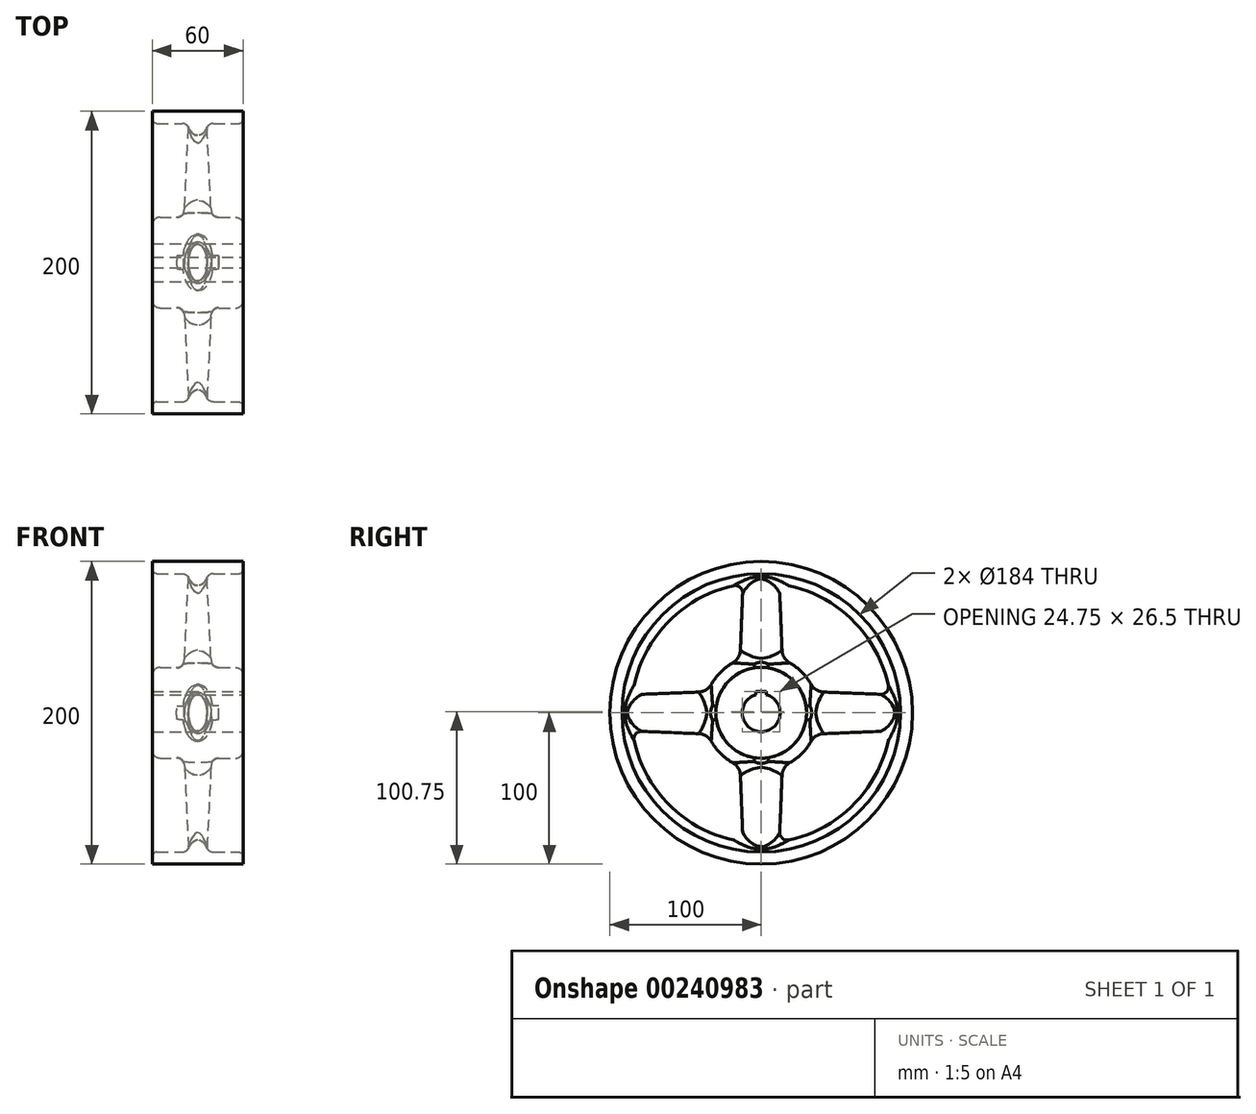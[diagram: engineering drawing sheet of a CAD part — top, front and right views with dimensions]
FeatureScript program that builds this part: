
annotation { "Feature Type Name" : "Feature", "Feature Type Description" : "" }
export const myFeature = defineFeature(function(context is Context, id is Id, definition is map)
    precondition{}
    {
        {
            var Q0;
            Q0=qCreatedBy(makeId("Front.planeOp"),FACE);
            var sketch = newSketch(context, id + "F0", { "sketchPlane" : qUnion([Q0])});
            skLineSegment(sketch, "E0", {"start": v(-30, 12.5) * mm, "end": v(30, 12.5) * mm});
            skLineSegment(sketch, "E1", {"start": v(30, 12.5) * mm, "end": v(30, 30) * mm});
            skLineSegment(sketch, "E2", {"start": v(30, 30) * mm, "end": v(10.58, 30) * mm});
            skLineSegment(sketch, "E3", {"start": v(-30, 30) * mm, "end": v(-30, 12.5) * mm});
            skLineSegment(sketch, "E4", {"start": v(-30, 100) * mm, "end": v(30, 100) * mm});
            skLineSegment(sketch, "E5", {"start": v(30, 100) * mm, "end": v(30, 92) * mm});
            skLineSegment(sketch, "E6", {"start": v(30, 92) * mm, "end": v(6.93, 92) * mm});
            skLineSegment(sketch, "E7", {"start": v(-30, 92) * mm, "end": v(-30, 100) * mm});
            skArc(sketch, "E8", {"start": v(10.58, 30) * mm, "mid": v(0, 38) * mm, "end": v(-10.58, 30) * mm});
            skLineSegment(sketch, "E9", {"start": v(-13.9, 38) * mm, "end": v(17.79, 38) * mm, "construction": true});
            skLineSegment(sketch, "E10", {"start": v(-13.9, 86) * mm, "end": v(17.79, 86) * mm, "construction": true});
            skArc(sketch, "E11", {"start": v(-6.93, 92) * mm, "mid": v(0, 86) * mm, "end": v(6.93, 92) * mm});
            skLineSegment(sketch, "E12.trimOffspring", {"start": v(-6.93, 92) * mm, "end": v(-30, 92) * mm});
            skLineSegment(sketch, "E13.trimOffspring", {"start": v(-10.58, 30) * mm, "end": v(-30, 30) * mm});
            skLineSegment(sketch, "E14", {"start": v(72.57, 0) * mm, "end": v(-63.68, 0) * mm, "construction": true});
            skSolve(sketch);
        }
        {
            var Q0;
            Q0=makeQuery(id+"F0.imprint","IMPRINT",FACE,{"disambiguationData":[TD([[makeQuery(id+"F0.imprint","IMPRINT",EDGE,{"derivedFrom":sQuery(id+"F0.wireOp",EDGE,"E0")}),1.0]])]});
            var Q1;
            Q1=makeQuery(id+"F0.imprint","IMPRINT",FACE,{"disambiguationData":[TD([[makeQuery(id+"F0.imprint","IMPRINT",EDGE,{"derivedFrom":sQuery(id+"F0.wireOp",EDGE,"E4")}),-1.0]])]});
            var Q2;
            Q2=sQuery(id+"F0.wireOp",EDGE,"E14");
            revolve(context, id + "F1", {"entities" : qUnion([Q0, Q1]), "axis" : qUnion([Q2]), "revolveType" : RevolveType.FULL});
        }
        {
            var Q0;
            Q0=qCreatedBy(makeId("Top.planeOp"),FACE);
            cPlane(context, id + "F2", {"entities" : qUnion([Q0]), "cplaneType" : CPlaneType.OFFSET, "offset" : 30 * mm, "width" : 150 * mm, "height" : 150 * mm});
        }
        {
            var Q0;
            Q0=qCreatedBy(makeId("Top.planeOp"),FACE);
            cPlane(context, id + "F3", {"entities" : qUnion([Q0]), "cplaneType" : CPlaneType.OFFSET, "offset" : 92 * mm, "width" : 150 * mm, "height" : 150 * mm});
        }
        {
            var Q0;
            Q0=qCreatedBy(id+"F2.planeOp",FACE);
            var sketch = newSketch(context, id + "F4", { "sketchPlane" : qUnion([Q0])});
            skCircle(sketch, "E15", {"center": v(0, 0) * mm, "radius": 38 * mm, "construction": true});
            skCircle(sketch, "E16", {"center": v(0, 0) * mm, "radius": 86 * mm, "construction": true});
            skLineSegment(sketch, "E17", {"start": v(-94.9, 11.6) * mm, "end": v(-23.99, 14.46) * mm, "construction": true});
            skPoint(sketch, "E18", {"position": v(-85.16, 12) * mm});
            skPoint(sketch, "E19", {"position": v(-35.33, 14) * mm});
            skLineSegment(sketch, "E20", {"start": v(-30, -33.26) * mm, "end": v(-30, 35.7) * mm, "construction": true});
            skLineSegment(sketch, "E21", {"start": v(-92, -48.52) * mm, "end": v(-92, 52.9) * mm, "construction": true});
            skPoint(sketch, "E22", {"position": v(-30, 14.21) * mm});
            skPoint(sketch, "E23", {"position": v(0, 14.21) * mm});
            skPoint(sketch, "E24", {"position": v(9, 0) * mm});
            skPoint(sketch, "E25", {"position": v(-9, 0) * mm});
            skPoint(sketch, "E26.MirrorP", {"position": v(0, -14.21) * mm});
            skEllipse(sketch, "E27", {"center": v(0, 0) * mm, "majorRadius": 14.21 * mm, "minorRadius": 9 * mm, "majorAxis": v(0, 1)});
            skPoint(sketch, "E28", {"position": v(-92, 11.73) * mm});
            skSolve(sketch);
        }
        {
            var Q0;
            Q0=qCreatedBy(id+"F3.planeOp",FACE);
            var sketch = newSketch(context, id + "F5", { "sketchPlane" : qUnion([Q0])});
            skPoint(sketch, "E29", {"position": v(-6, 0) * mm});
            skPoint(sketch, "E30", {"position": v(6, 0) * mm});
            skPoint(sketch, "E31", {"position": v(0, 11.73) * mm});
            skPoint(sketch, "E32.MirrorP", {"position": v(0, -11.73) * mm});
            skEllipse(sketch, "E33", {"center": v(0, 0) * mm, "majorRadius": 11.73 * mm, "minorRadius": 6 * mm, "majorAxis": v(0, 1)});
            skSolve(sketch);
        }
        {
            var Q0;
            Q0=makeQuery(id+"F4.imprint","IMPRINT",FACE,{"disambiguationData":[TD([[makeQuery(id+"F4.imprint","IMPRINT",EDGE,{"derivedFrom":sQuery(id+"F4.wireOp",EDGE,"E27")}),1.0]])]});
            var Q1;
            Q1=makeQuery(id+"F5.imprint","IMPRINT",FACE,{"disambiguationData":[TD([[makeQuery(id+"F5.imprint","IMPRINT",EDGE,{"derivedFrom":sQuery(id+"F5.wireOp",EDGE,"E33")}),1.0]])]});
            loft(context, id + "F6", {"sheetProfilesArray" : [{ "sheetProfileEntities" : qUnion([Q0]) }, { "sheetProfileEntities" : qUnion([Q1]) }]});
        }
        {
            var Q0;
            Q0=makeQuery(id+"F6.opLoft","SWEPT_BODY",BODY,{"disambiguationData":[OSD([makeQuery(id+"F4.imprint","IMPRINT",FACE,{"disambiguationData":[TD([[makeQuery(id+"F4.imprint","IMPRINT",EDGE,{"derivedFrom":sQuery(id+"F4.wireOp",EDGE,"E27")}),1.0]])]}),makeQuery(id+"F5.imprint","IMPRINT",FACE,{"disambiguationData":[TD([[makeQuery(id+"F5.imprint","IMPRINT",EDGE,{"derivedFrom":sQuery(id+"F5.wireOp",EDGE,"E33")}),1.0]])]})])]});
            var Q1;
            Q1=sQuery(id+"F0.wireOp",EDGE,"E14");
            circularPattern(context, id + "F7", {"entities" : qUnion([Q0]), "axis" : qUnion([Q1]), "angle" : 360 * degree, "instanceCount" : 4, "equalSpace" : true});
        }
        {
            var Q0;
            Q0=makeQuery(id+"F1.opRevolve","SWEPT_BODY",BODY,{"disambiguationData":[OSD([sQuery(id+"F0.wireOp",EDGE,"E0"),sQuery(id+"F0.wireOp",EDGE,"E1"),sQuery(id+"F0.wireOp",EDGE,"E2"),sQuery(id+"F0.wireOp",EDGE,"E3"),sQuery(id+"F0.wireOp",EDGE,"E8"),sQuery(id+"F0.wireOp",EDGE,"E13.trimOffspring")])]});
            var Q1;
            Q1=makeQuery(id+"F6.opLoft","SWEPT_BODY",BODY,{"disambiguationData":[OSD([makeQuery(id+"F4.imprint","IMPRINT",FACE,{"disambiguationData":[TD([[makeQuery(id+"F4.imprint","IMPRINT",EDGE,{"derivedFrom":sQuery(id+"F4.wireOp",EDGE,"E27")}),1.0]])]}),makeQuery(id+"F5.imprint","IMPRINT",FACE,{"disambiguationData":[TD([[makeQuery(id+"F5.imprint","IMPRINT",EDGE,{"derivedFrom":sQuery(id+"F5.wireOp",EDGE,"E33")}),1.0]])]})])]});
            var Q2;
            Q2=makeQuery(id+"F7.opPattern","COPY",BODY,{"derivedFrom":makeQuery(id+"F6.opLoft","SWEPT_BODY",BODY,{"disambiguationData":[OSD([makeQuery(id+"F4.imprint","IMPRINT",FACE,{"disambiguationData":[TD([[makeQuery(id+"F4.imprint","IMPRINT",EDGE,{"derivedFrom":sQuery(id+"F4.wireOp",EDGE,"E27")}),1.0]])]}),makeQuery(id+"F5.imprint","IMPRINT",FACE,{"disambiguationData":[TD([[makeQuery(id+"F5.imprint","IMPRINT",EDGE,{"derivedFrom":sQuery(id+"F5.wireOp",EDGE,"E33")}),1.0]])]})])]}),"instanceName":"2"});
            var Q3;
            Q3=makeQuery(id+"F7.opPattern","COPY",BODY,{"derivedFrom":makeQuery(id+"F6.opLoft","SWEPT_BODY",BODY,{"disambiguationData":[OSD([makeQuery(id+"F4.imprint","IMPRINT",FACE,{"disambiguationData":[TD([[makeQuery(id+"F4.imprint","IMPRINT",EDGE,{"derivedFrom":sQuery(id+"F4.wireOp",EDGE,"E27")}),1.0]])]}),makeQuery(id+"F5.imprint","IMPRINT",FACE,{"disambiguationData":[TD([[makeQuery(id+"F5.imprint","IMPRINT",EDGE,{"derivedFrom":sQuery(id+"F5.wireOp",EDGE,"E33")}),1.0]])]})])]}),"instanceName":"3"});
            var Q4;
            Q4=makeQuery(id+"F7.opPattern","COPY",BODY,{"derivedFrom":makeQuery(id+"F6.opLoft","SWEPT_BODY",BODY,{"disambiguationData":[OSD([makeQuery(id+"F4.imprint","IMPRINT",FACE,{"disambiguationData":[TD([[makeQuery(id+"F4.imprint","IMPRINT",EDGE,{"derivedFrom":sQuery(id+"F4.wireOp",EDGE,"E27")}),1.0]])]}),makeQuery(id+"F5.imprint","IMPRINT",FACE,{"disambiguationData":[TD([[makeQuery(id+"F5.imprint","IMPRINT",EDGE,{"derivedFrom":sQuery(id+"F5.wireOp",EDGE,"E33")}),1.0]])]})])]}),"instanceName":"1"});
            var Q5;
            Q5=makeQuery(id+"F1.opRevolve","SWEPT_BODY",BODY,{"disambiguationData":[OSD([sQuery(id+"F0.wireOp",EDGE,"E4"),sQuery(id+"F0.wireOp",EDGE,"E5"),sQuery(id+"F0.wireOp",EDGE,"E6"),sQuery(id+"F0.wireOp",EDGE,"E7"),sQuery(id+"F0.wireOp",EDGE,"E11"),sQuery(id+"F0.wireOp",EDGE,"E12.trimOffspring")])]});
            booleanBodies(context, id + "F8", {"operationType" : BooleanOperationType.UNION, "tools" : qUnion([Q0, Q1, Q2, Q3, Q4, Q5])});
        }
        {
            var Q0;
            Q0=makeQuery(id+"F1.opRevolve","SWEPT_FACE",FACE,{"disambiguationData":[OSD([sQuery(id+"F0.wireOp",EDGE,"E1")])]});
            var sketch = newSketch(context, id + "F9", { "sketchPlane" : qUnion([Q0])});
            skLineSegment(sketch, "E34.bottom", {"start": v(3.5, 14) * mm, "end": v(-3.5, 14) * mm});
            skLineSegment(sketch, "E34.top", {"start": v(3.5, 10) * mm, "end": v(-3.5, 10) * mm});
            skLineSegment(sketch, "E34.left", {"start": v(3.5, 14) * mm, "end": v(3.5, 10) * mm});
            skLineSegment(sketch, "E34.right", {"start": v(-3.5, 14) * mm, "end": v(-3.5, 10) * mm});
            skPoint(sketch, "E34.middle", {"position": v(0, 12) * mm});
            skSolve(sketch);
        }
        {
            var Q0;
            Q0 = qSketchRegion(id + "F9", true);
            extrude(context, id + "F10", {"entities" : qUnion([Q0]), "operationType" : NewBodyOperationType.REMOVE, "endBound" : BoundingType.THROUGH_ALL, "oppositeDirection" : true, "depth" : 25 * mm});
        }
        {
            var Q0;
            Q0=makeQuery(id+"F8.opBoolean","INTERSECT",EDGE,{"derivedFrom":[makeQuery(id+"F1.opRevolve","SWEPT_FACE",FACE,{"disambiguationData":[OSD([sQuery(id+"F0.wireOp",EDGE,"E11")])]}),makeQuery(id+"F6.opLoft","SWEPT_FACE",FACE,{"disambiguationData":[OSD([sQuery(id+"F4.wireOp",EDGE,"E27"),sQuery(id+"F5.wireOp",EDGE,"E33")])]})]});
            var Q1;
            Q1=makeQuery(id+"F8.opBoolean","INTERSECT",EDGE,{"derivedFrom":[makeQuery(id+"F1.opRevolve","SWEPT_FACE",FACE,{"disambiguationData":[OSD([sQuery(id+"F0.wireOp",EDGE,"E11")])]}),makeQuery(id+"F7.opPattern","COPY",FACE,{"derivedFrom":makeQuery(id+"F6.opLoft","SWEPT_FACE",FACE,{"disambiguationData":[OSD([sQuery(id+"F4.wireOp",EDGE,"E27"),sQuery(id+"F5.wireOp",EDGE,"E33")])]}),"instanceName":"1"})]});
            var Q2;
            Q2=makeQuery(id+"F8.opBoolean","INTERSECT",EDGE,{"derivedFrom":[makeQuery(id+"F1.opRevolve","SWEPT_FACE",FACE,{"disambiguationData":[OSD([sQuery(id+"F0.wireOp",EDGE,"E11")])]}),makeQuery(id+"F7.opPattern","COPY",FACE,{"derivedFrom":makeQuery(id+"F6.opLoft","SWEPT_FACE",FACE,{"disambiguationData":[OSD([sQuery(id+"F4.wireOp",EDGE,"E27"),sQuery(id+"F5.wireOp",EDGE,"E33")])]}),"instanceName":"2"})]});
            var Q3;
            Q3=makeQuery(id+"F8.opBoolean","INTERSECT",EDGE,{"derivedFrom":[makeQuery(id+"F1.opRevolve","SWEPT_FACE",FACE,{"disambiguationData":[OSD([sQuery(id+"F0.wireOp",EDGE,"E11")])]}),makeQuery(id+"F7.opPattern","COPY",FACE,{"derivedFrom":makeQuery(id+"F6.opLoft","SWEPT_FACE",FACE,{"disambiguationData":[OSD([sQuery(id+"F4.wireOp",EDGE,"E27"),sQuery(id+"F5.wireOp",EDGE,"E33")])]}),"instanceName":"3"})]});
            fillet(context, id + "F11", {"entities" : qUnion([Q0, Q1, Q2, Q3]), "radius" : 5 * mm, "tangentPropagation" : true, "allowEdgeOverflow" : false});
        }
        {
            var Q0;
            Q0=makeQuery(id+"F8.opBoolean","INTERSECT",EDGE,{"derivedFrom":[makeQuery(id+"F1.opRevolve","SWEPT_FACE",FACE,{"disambiguationData":[OSD([sQuery(id+"F0.wireOp",EDGE,"E8")])]}),makeQuery(id+"F7.opPattern","COPY",FACE,{"derivedFrom":makeQuery(id+"F6.opLoft","SWEPT_FACE",FACE,{"disambiguationData":[OSD([sQuery(id+"F4.wireOp",EDGE,"E27"),sQuery(id+"F5.wireOp",EDGE,"E33")])]}),"instanceName":"1"})]});
            var Q1;
            Q1=makeQuery(id+"F8.opBoolean","INTERSECT",EDGE,{"derivedFrom":[makeQuery(id+"F1.opRevolve","SWEPT_FACE",FACE,{"disambiguationData":[OSD([sQuery(id+"F0.wireOp",EDGE,"E8")])]}),makeQuery(id+"F6.opLoft","SWEPT_FACE",FACE,{"disambiguationData":[OSD([sQuery(id+"F4.wireOp",EDGE,"E27"),sQuery(id+"F5.wireOp",EDGE,"E33")])]})]});
            var Q2;
            Q2=makeQuery(id+"F8.opBoolean","INTERSECT",EDGE,{"derivedFrom":[makeQuery(id+"F1.opRevolve","SWEPT_FACE",FACE,{"disambiguationData":[OSD([sQuery(id+"F0.wireOp",EDGE,"E8")])]}),makeQuery(id+"F7.opPattern","COPY",FACE,{"derivedFrom":makeQuery(id+"F6.opLoft","SWEPT_FACE",FACE,{"disambiguationData":[OSD([sQuery(id+"F4.wireOp",EDGE,"E27"),sQuery(id+"F5.wireOp",EDGE,"E33")])]}),"instanceName":"3"})]});
            var Q3;
            Q3=makeQuery(id+"F8.opBoolean","INTERSECT",EDGE,{"derivedFrom":[makeQuery(id+"F1.opRevolve","SWEPT_FACE",FACE,{"disambiguationData":[OSD([sQuery(id+"F0.wireOp",EDGE,"E8")])]}),makeQuery(id+"F7.opPattern","COPY",FACE,{"derivedFrom":makeQuery(id+"F6.opLoft","SWEPT_FACE",FACE,{"disambiguationData":[OSD([sQuery(id+"F4.wireOp",EDGE,"E27"),sQuery(id+"F5.wireOp",EDGE,"E33")])]}),"instanceName":"2"})]});
            fillet(context, id + "F12", {"entities" : qUnion([Q0, Q1, Q2, Q3]), "radius" : 10 * mm, "tangentPropagation" : true, "allowEdgeOverflow" : false});
        }
        {
            var Q0;
            Q0=makeQuery(id+"F1.opRevolve","SWEPT_EDGE",EDGE,{"disambiguationData":[OSD([sQuery(id+"F0.wireOp",EDGE,"E8"),sQuery(id+"F0.wireOp",EDGE,"E13.trimOffspring")])]});
            var Q1;
            Q1=makeQuery(id+"F1.opRevolve","SWEPT_EDGE",EDGE,{"disambiguationData":[OSD([sQuery(id+"F0.wireOp",EDGE,"E2"),sQuery(id+"F0.wireOp",EDGE,"E8")])]});
            var Q2;
            Q2=makeQuery(id+"F1.opRevolve","SWEPT_EDGE",EDGE,{"disambiguationData":[OSD([sQuery(id+"F0.wireOp",EDGE,"E6"),sQuery(id+"F0.wireOp",EDGE,"E11")])]});
            var Q3;
            Q3=makeQuery(id+"F1.opRevolve","SWEPT_EDGE",EDGE,{"disambiguationData":[OSD([sQuery(id+"F0.wireOp",EDGE,"E11"),sQuery(id+"F0.wireOp",EDGE,"E12.trimOffspring")])]});
            fillet(context, id + "F13", {"entities" : qUnion([Q0, Q1, Q2, Q3]), "radius" : 5 * mm, "tangentPropagation" : true, "allowEdgeOverflow" : false});
        }
        {
            var Q0;
            Q0=makeQuery(id+"F1.opRevolve","SWEPT_EDGE",EDGE,{"disambiguationData":[OSD([sQuery(id+"F0.wireOp",EDGE,"E3"),sQuery(id+"F0.wireOp",EDGE,"E13.trimOffspring")])]});
            var Q1;
            Q1=makeQuery(id+"F1.opRevolve","SWEPT_EDGE",EDGE,{"disambiguationData":[OSD([sQuery(id+"F0.wireOp",EDGE,"E1"),sQuery(id+"F0.wireOp",EDGE,"E2")])]});
            fillet(context, id + "F14", {"entities" : qUnion([Q0, Q1]), "radius" : 5 * mm, "tangentPropagation" : true, "allowEdgeOverflow" : false});
        }
        {
            var Q0;
            Q0=makeQuery(id+"F1.opRevolve","SWEPT_EDGE",EDGE,{"disambiguationData":[OSD([sQuery(id+"F0.wireOp",EDGE,"E7"),sQuery(id+"F0.wireOp",EDGE,"E12.trimOffspring")])]});
            var Q1;
            Q1=makeQuery(id+"F1.opRevolve","SWEPT_EDGE",EDGE,{"disambiguationData":[OSD([sQuery(id+"F0.wireOp",EDGE,"E5"),sQuery(id+"F0.wireOp",EDGE,"E6")])]});
            fillet(context, id + "F15", {"entities" : qUnion([Q0, Q1]), "radius" : 3 * mm, "tangentPropagation" : true, "allowEdgeOverflow" : false});
        }
        {
            var Q0;
            Q0=makeQuery(id+"F10.boolean.opBoolean","COPY",EDGE,{"derivedFrom":makeQuery(id+"F10.opExtrude","SWEPT_EDGE",EDGE,{"disambiguationData":[OSD([sQuery(id+"F9.wireOp",EDGE,"E34.bottom"),sQuery(id+"F9.wireOp",EDGE,"E34.left")])]})});
            var Q1;
            Q1=makeQuery(id+"F10.boolean.opBoolean","COPY",EDGE,{"derivedFrom":makeQuery(id+"F10.opExtrude","SWEPT_EDGE",EDGE,{"disambiguationData":[OSD([sQuery(id+"F9.wireOp",EDGE,"E34.bottom"),sQuery(id+"F9.wireOp",EDGE,"E34.right")])]})});
            fillet(context, id + "F16", {"entities" : qUnion([Q0, Q1]), "radius" : 0.2 * mm, "tangentPropagation" : true, "allowEdgeOverflow" : false});
        }
    });
